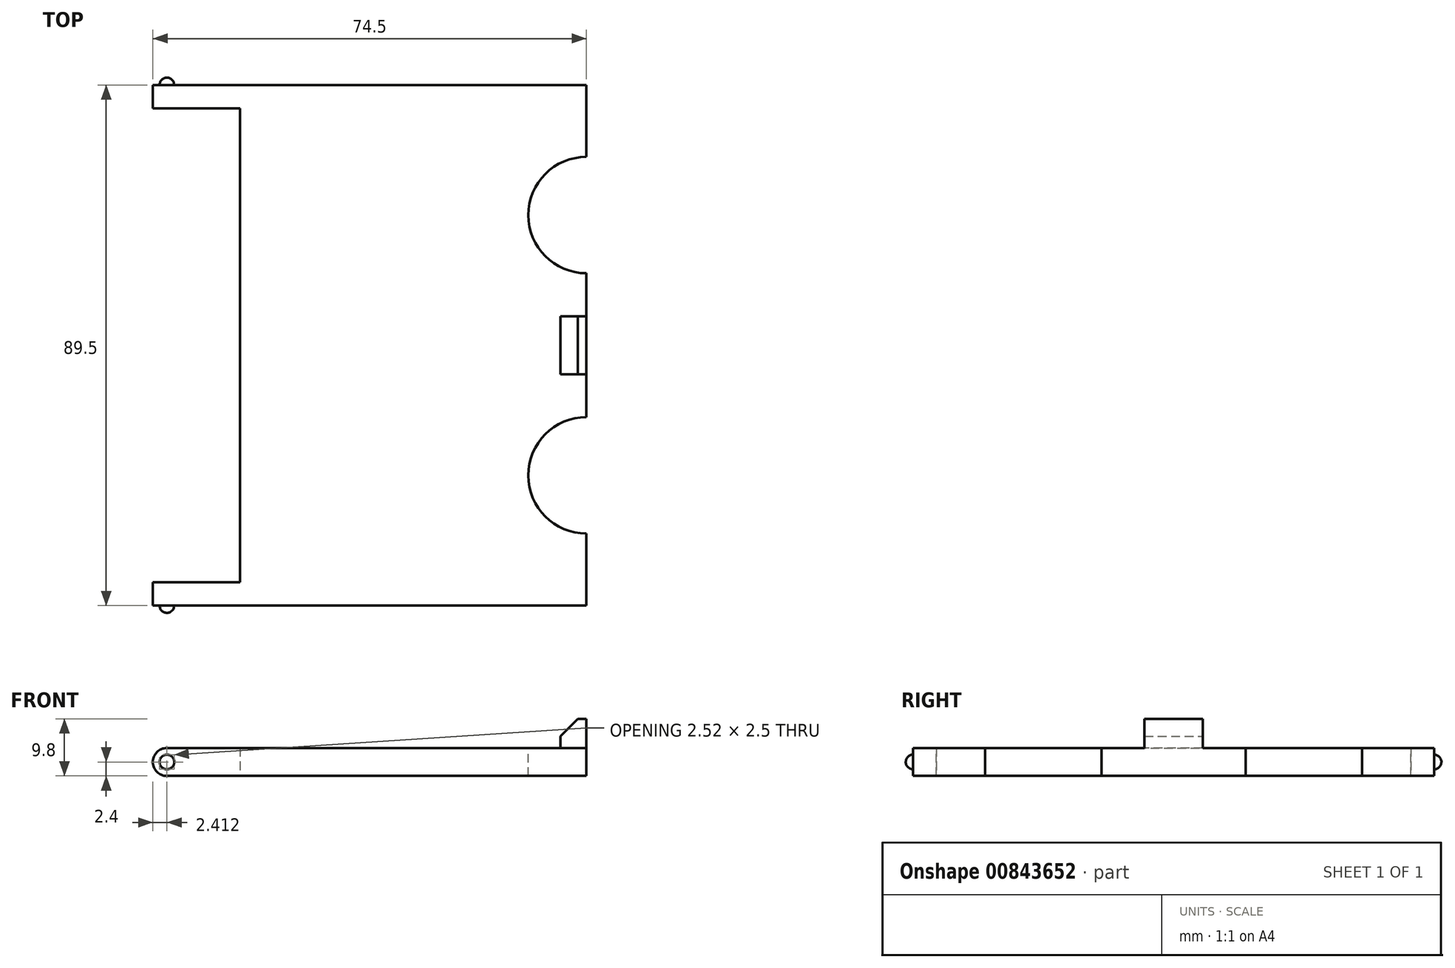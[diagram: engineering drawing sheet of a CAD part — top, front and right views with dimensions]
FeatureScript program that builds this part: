
annotation { "Feature Type Name" : "Feature", "Feature Type Description" : "" }
export const myFeature = defineFeature(function(context is Context, id is Id, definition is map)
    precondition{}
    {
        {
            var Q0;
            Q0=qCreatedBy(makeId("Top.planeOp"),FACE);
            var sketch = newSketch(context, id + "F0", { "sketchPlane" : qUnion([Q0])});
            skLineSegment(sketch, "E0.bottom", {"start": v(-37.25, -44.75) * mm, "end": v(37.25, -44.75) * mm});
            skLineSegment(sketch, "E0.top", {"start": v(-37.25, 44.75) * mm, "end": v(37.25, 44.75) * mm});
            skLineSegment(sketch, "E0.left", {"start": v(-37.25, -44.75) * mm, "end": v(-37.25, -40.75) * mm});
            skLineSegment(sketch, "E0.right", {"start": v(37.25, -44.75) * mm, "end": v(37.25, 44.75) * mm});
            skPoint(sketch, "E0.middle", {"position": v(0, 0) * mm});
            skLineSegment(sketch, "E1.bottom", {"start": v(-37.25, -40.75) * mm, "end": v(-22.25, -40.75) * mm});
            skLineSegment(sketch, "E1.top", {"start": v(-37.25, 40.75) * mm, "end": v(-22.25, 40.75) * mm});
            skLineSegment(sketch, "E1.right", {"start": v(-22.25, -40.75) * mm, "end": v(-22.25, 40.75) * mm});
            skLineSegment(sketch, "E2.trimOffspring", {"start": v(-37.25, 40.75) * mm, "end": v(-37.25, 44.75) * mm});
            skSolve(sketch);
        }
        {
            var Q0;
            Q0 = qSketchRegion(id + "F0", true);
            extrude(context, id + "F1", {"entities" : qUnion([Q0]), "depth" : 4.8 * mm, "offsetDistance" : 25 * mm});
        }
        {
            var Q0;
            Q0=makeQuery(id+"F1.opExtrude","SWEPT_FACE",FACE,{"disambiguationData":[OSD([sQuery(id+"F0.wireOp",EDGE,"E0.bottom")])]});
            var sketch = newSketch(context, id + "F2", { "sketchPlane" : qUnion([Q0])});
            skCircle(sketch, "E3", {"center": v(-34.85, 2.4) * mm, "radius": 2.4 * mm});
            skArc(sketch, "E4", {"start": v(-34.84, 3.65) * mm, "mid": v(-36.1, 2.4) * mm, "end": v(-34.84, 1.15) * mm});
            skLineSegment(sketch, "E5", {"start": v(-34.84, 3.65) * mm, "end": v(-34.84, 1.15) * mm});
            skSolve(sketch);
        }
        {
            var Q0;
            Q0=makeQuery(id+"F2.imprint","IMPRINT",FACE,{"disambiguationData":[TD([[makeQuery(id+"F2.imprint","IMPRINT",EDGE,{"derivedFrom":sQuery(id+"F2.wireOp",EDGE,"E4")}),1.0]])]});
            var Q1;
            Q1=sQuery(id+"F2.wireOp",EDGE,"E5");
            revolve(context, id + "F3", {"operationType" : NewBodyOperationType.ADD, "surfaceOperationType" : NewSurfaceOperationType.NEW, "entities" : qUnion([Q0]), "axis" : qUnion([Q1]), "revolveType" : RevolveType.FULL});
        }
        {
            var Q0;
            Q0=makeQuery(id+"F1.opExtrude","SWEPT_BODY",BODY,{"disambiguationData":[OSD([sQuery(id+"F0.wireOp",EDGE,"E0.bottom"),sQuery(id+"F0.wireOp",EDGE,"E0.top"),sQuery(id+"F0.wireOp",EDGE,"E0.left"),sQuery(id+"F0.wireOp",EDGE,"E0.right"),sQuery(id+"F0.wireOp",EDGE,"E1.bottom"),sQuery(id+"F0.wireOp",EDGE,"E1.top"),sQuery(id+"F0.wireOp",EDGE,"E1.right"),sQuery(id+"F0.wireOp",EDGE,"E2.trimOffspring")])]});
            var Q1;
            Q1=qCreatedBy(makeId("Front.planeOp"),FACE);
            mirror(context, id + "F4", {"operationType" : NewBodyOperationType.ADD, "entities" : qUnion([Q0]), "mirrorPlane" : qUnion([Q1])});
        }
        {
            var Q0;
            Q0=makeQuery(id+"F1.opExtrude","CAP_FACE",FACE,{"disambiguationData":[OSD([sQuery(id+"F0.wireOp",EDGE,"E0.bottom"),sQuery(id+"F0.wireOp",EDGE,"E0.top"),sQuery(id+"F0.wireOp",EDGE,"E0.left"),sQuery(id+"F0.wireOp",EDGE,"E0.right"),sQuery(id+"F0.wireOp",EDGE,"E1.bottom"),sQuery(id+"F0.wireOp",EDGE,"E1.top"),sQuery(id+"F0.wireOp",EDGE,"E1.right"),sQuery(id+"F0.wireOp",EDGE,"E2.trimOffspring")])],"isStart":false});
            var sketch = newSketch(context, id + "F5", { "sketchPlane" : qUnion([Q0])});
            skPoint(sketch, "E6", {"position": v(37.25, 22.37) * mm});
            skCircle(sketch, "E7", {"center": v(37.25, 22.37) * mm, "radius": 10 * mm});
            skCircle(sketch, "E8.MirrorC", {"center": v(37.25, -22.37) * mm, "radius": 10 * mm});
            skSolve(sketch);
        }
        {
            var Q0;
            Q0 = qSketchRegion(id + "F5", true);
            extrude(context, id + "F6", {"entities" : qUnion([Q0]), "operationType" : NewBodyOperationType.REMOVE, "endBound" : BoundingType.THROUGH_ALL, "oppositeDirection" : true, "depth" : 25 * mm, "offsetDistance" : 25 * mm});
        }
        {
            var Q0;
            Q0=makeQuery(id+"F1.opExtrude","CAP_FACE",FACE,{"disambiguationData":[OSD([sQuery(id+"F0.wireOp",EDGE,"E0.bottom"),sQuery(id+"F0.wireOp",EDGE,"E0.top"),sQuery(id+"F0.wireOp",EDGE,"E0.left"),sQuery(id+"F0.wireOp",EDGE,"E0.right"),sQuery(id+"F0.wireOp",EDGE,"E1.bottom"),sQuery(id+"F0.wireOp",EDGE,"E1.top"),sQuery(id+"F0.wireOp",EDGE,"E1.right"),sQuery(id+"F0.wireOp",EDGE,"E2.trimOffspring")])],"isStart":false});
            var sketch = newSketch(context, id + "F7", { "sketchPlane" : qUnion([Q0])});
            skLineSegment(sketch, "E9.bottom", {"start": v(37.25, 5) * mm, "end": v(32.75, 5) * mm});
            skLineSegment(sketch, "E9.top", {"start": v(37.25, -5) * mm, "end": v(32.75, -5) * mm});
            skLineSegment(sketch, "E9.left", {"start": v(37.25, 5) * mm, "end": v(37.25, -5) * mm});
            skLineSegment(sketch, "E9.right", {"start": v(32.75, 5) * mm, "end": v(32.75, -5) * mm});
            skPoint(sketch, "E10", {"position": v(32.75, 0) * mm});
            skSolve(sketch);
        }
        {
            var Q0;
            Q0=makeQuery(id+"F7.imprint","IMPRINT",FACE,{"disambiguationData":[TD([[makeQuery(id+"F7.imprint","IMPRINT",EDGE,{"derivedFrom":sQuery(id+"F7.wireOp",EDGE,"E9.bottom")}),1.0]])]});
            extrude(context, id + "F8", {"entities" : qUnion([Q0]), "operationType" : NewBodyOperationType.ADD, "depth" : 5 * mm, "offsetDistance" : 25 * mm});
        }
        {
            var Q0;
            Q0=makeQuery(id+"F8.opExtrude","CAP_EDGE",EDGE,{"disambiguationData":[OSD([sQuery(id+"F7.wireOp",EDGE,"E9.right")])],"isStart":false});
            chamfer(context, id + "F9", {"entities" : qUnion([Q0]), "width" : 3 * mm, "tangentPropagation" : true});
        }
        {
            var Q0;
            {var subQ0=sQuery(id+"F2.wireOp",EDGE,"E3");var subQ1=sQuery(id+"F0.wireOp",EDGE,"E0.bottom");var subQ4=makeQuery(id+"F1.opExtrude","CAP_EDGE",EDGE,{"disambiguationData":[OSD([subQ1])],"isStart":false});var subQ5=makeQuery(id+"F2.imprint","INTERSECT",VERTEX,{"derivedFrom":[subQ4,subQ0]});Q0=makeQuery(id+"F2.imprint","IMPRINT",FACE,{"disambiguationData":[TD([[makeQuery(id+"F2.imprint","IMPRINT",EDGE,{"disambiguationData":[TD([[subQ5,-1.0]])],"derivedFrom":subQ0}),-1.0]])]});}
            var Q1;
            {var subQ0=sQuery(id+"F2.wireOp",EDGE,"E3");var subQ1=sQuery(id+"F0.wireOp",EDGE,"E0.bottom");var subQ4=makeQuery(id+"F1.opExtrude","CAP_EDGE",EDGE,{"disambiguationData":[OSD([subQ1])],"isStart":true});var subQ5=makeQuery(id+"F2.imprint","INTERSECT",VERTEX,{"derivedFrom":[subQ4,subQ0]});Q1=makeQuery(id+"F2.imprint","IMPRINT",FACE,{"disambiguationData":[TD([[makeQuery(id+"F2.imprint","IMPRINT",EDGE,{"disambiguationData":[TD([[subQ5,1.0]])],"derivedFrom":subQ0}),-1.0]])]});}
            extrude(context, id + "F10", {"entities" : qUnion([Q0, Q1]), "operationType" : NewBodyOperationType.REMOVE, "endBound" : BoundingType.THROUGH_ALL, "oppositeDirection" : true, "depth" : 25 * mm, "offsetDistance" : 25 * mm});
        }
    });
